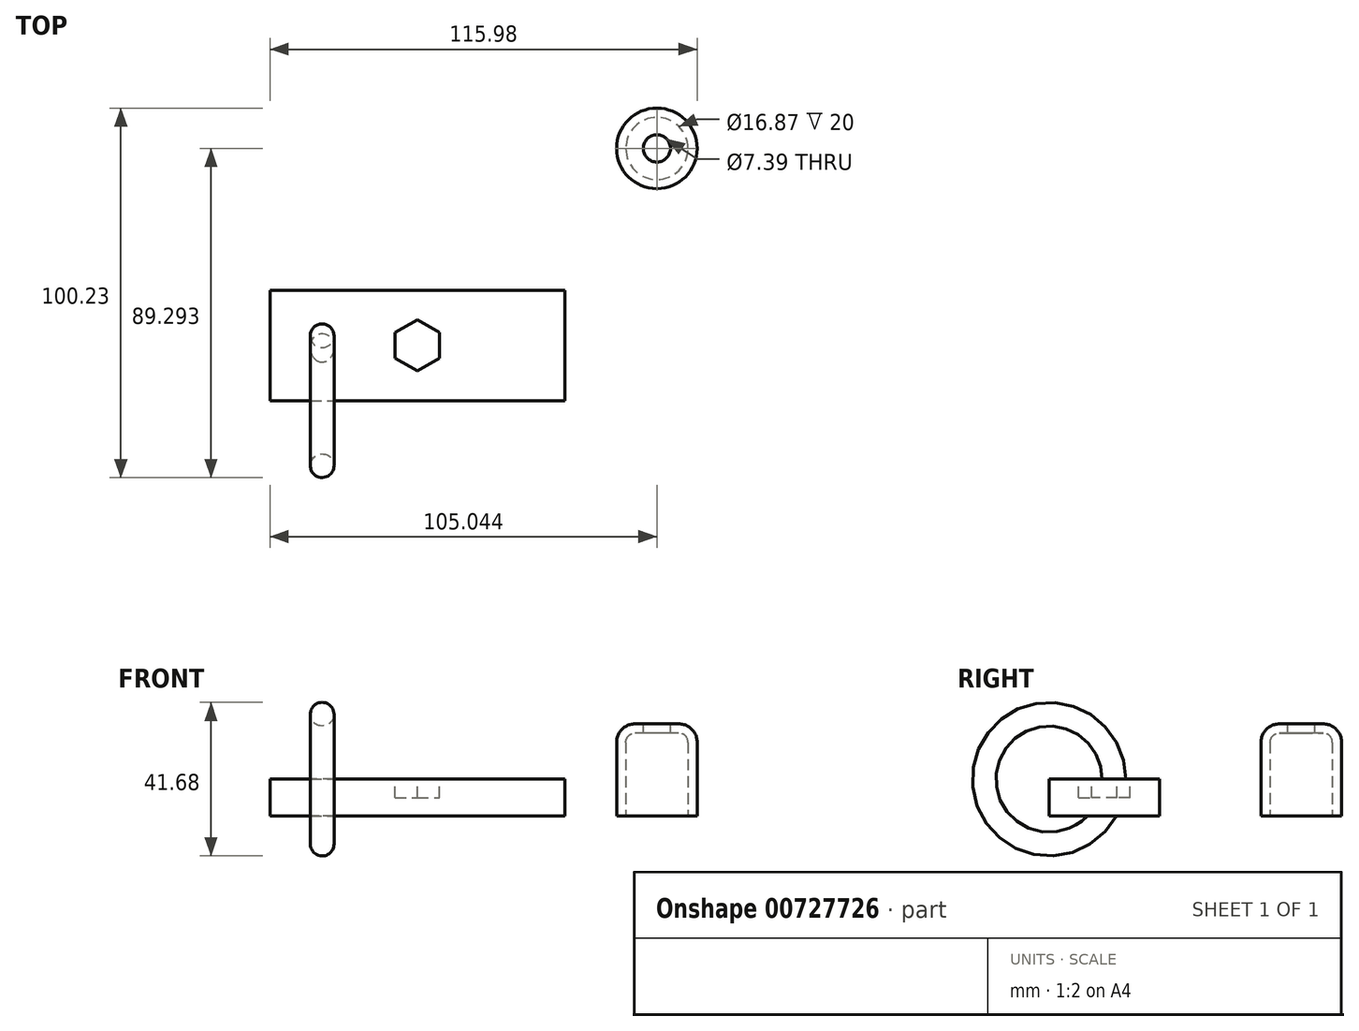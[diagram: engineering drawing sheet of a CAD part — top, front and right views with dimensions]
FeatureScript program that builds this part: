
annotation { "Feature Type Name" : "Feature", "Feature Type Description" : "" }
export const myFeature = defineFeature(function(context is Context, id is Id, definition is map)
    precondition{}
    {
        {
            var Q0;
            Q0=qCreatedBy(makeId("Top.planeOp"),FACE);
            var sketch = newSketch(context, id + "F0", { "sketchPlane" : qUnion([Q0])});
            skLineSegment(sketch, "E0.bottom", {"start": v(-40, -15) * mm, "end": v(40, -15) * mm});
            skLineSegment(sketch, "E0.top", {"start": v(-40, 15) * mm, "end": v(40, 15) * mm});
            skLineSegment(sketch, "E0.left", {"start": v(-40, -15) * mm, "end": v(-40, 15) * mm});
            skLineSegment(sketch, "E0.right", {"start": v(40, -15) * mm, "end": v(40, 15) * mm});
            skPoint(sketch, "E1", {"position": v(-40, 0) * mm});
            skPoint(sketch, "E2", {"position": v(0, -15) * mm});
            skSolve(sketch);
        }
        {
            var Q0;
            Q0=makeQuery(id+"F0.imprint","IMPRINT",FACE,{"disambiguationData":[TD([[makeQuery(id+"F0.imprint","IMPRINT",EDGE,{"derivedFrom":sQuery(id+"F0.wireOp",EDGE,"E0.bottom")}),1.0]])]});
            extrude(context, id + "F1", {"entities" : qUnion([Q0]), "depth" : 10 * mm, "offsetDistance" : 25 * mm});
        }
        {
            var Q0;
            Q0=makeQuery(id+"F1.opExtrude","CAP_FACE",FACE,{"disambiguationData":[OSD([sQuery(id+"F0.wireOp",EDGE,"E0.bottom"),sQuery(id+"F0.wireOp",EDGE,"E0.top"),sQuery(id+"F0.wireOp",EDGE,"E0.left"),sQuery(id+"F0.wireOp",EDGE,"E0.right")])],"isStart":false});
            var sketch = newSketch(context, id + "F2", { "sketchPlane" : qUnion([Q0])});
            skCircle(sketch, "E3.cCircle", {"center": v(0, 0) * mm, "radius": 6 * mm, "construction": true});
            skLineSegment(sketch, "E3.0", {"start": v(6, 3.46) * mm, "end": v(6, -3.46) * mm});
            skLineSegment(sketch, "E3.1", {"start": v(6, -3.46) * mm, "end": v(0, -6.93) * mm});
            skLineSegment(sketch, "E3.2", {"start": v(0, -6.93) * mm, "end": v(-6, -3.46) * mm});
            skLineSegment(sketch, "E3.3", {"start": v(-6, -3.46) * mm, "end": v(-6, 3.46) * mm});
            skLineSegment(sketch, "E3.4", {"start": v(-6, 3.46) * mm, "end": v(0, 6.93) * mm});
            skLineSegment(sketch, "E3.5", {"start": v(0, 6.93) * mm, "end": v(6, 3.46) * mm});
            skPoint(sketch, "E3.0.midPoint", {"position": v(6, 0) * mm});
            skSolve(sketch);
        }
        {
            var Q0;
            Q0=makeQuery(id+"F2.imprint","IMPRINT",FACE,{"disambiguationData":[TD([[makeQuery(id+"F2.imprint","IMPRINT",EDGE,{"derivedFrom":sQuery(id+"F2.wireOp",EDGE,"E3.0")}),-1.0]])]});
            extrude(context, id + "F3", {"entities" : qUnion([Q0]), "operationType" : NewBodyOperationType.REMOVE, "oppositeDirection" : true, "depth" : 5 * mm, "offsetDistance" : 25 * mm});
        }
        {
            var Q0;
            Q0=makeQuery(id+"F1.opExtrude","CAP_FACE",FACE,{"disambiguationData":[OSD([sQuery(id+"F0.wireOp",EDGE,"E0.bottom"),sQuery(id+"F0.wireOp",EDGE,"E0.top"),sQuery(id+"F0.wireOp",EDGE,"E0.left"),sQuery(id+"F0.wireOp",EDGE,"E0.right")])],"isStart":false});
            var sketch = newSketch(context, id + "F4", { "sketchPlane" : qUnion([Q0])});
            skCircle(sketch, "E4", {"center": v(-25.82, 2.63) * mm, "radius": 3.21 * mm});
            skSolve(sketch);
        }
        {
            var Q0;
            Q0=makeQuery(id+"F4.imprint","IMPRINT",FACE,{"disambiguationData":[TD([[makeQuery(id+"F4.imprint","IMPRINT",EDGE,{"derivedFrom":sQuery(id+"F4.wireOp",EDGE,"E4")}),1.0]])]});
            var Q1;
            Q1=makeQuery(id+"F1.opExtrude","CAP_EDGE",EDGE,{"disambiguationData":[OSD([sQuery(id+"F0.wireOp",EDGE,"E0.bottom")])],"isStart":false});
            revolve(context, id + "F5", {"operationType" : NewBodyOperationType.ADD, "surfaceOperationType" : NewSurfaceOperationType.NEW, "entities" : qUnion([Q0]), "axis" : qUnion([Q1]), "revolveType" : RevolveType.FULL});
        }
        {
            var Q0;
            Q0=qCreatedBy(makeId("Top.planeOp"),FACE);
            var sketch = newSketch(context, id + "F6", { "sketchPlane" : qUnion([Q0])});
            skCircle(sketch, "E5", {"center": v(65.04, 53.45) * mm, "radius": 10.94 * mm});
            skSolve(sketch);
        }
        {
            var Q0;
            Q0=makeQuery(id+"F6.imprint","IMPRINT",FACE,{"disambiguationData":[TD([[makeQuery(id+"F6.imprint","IMPRINT",EDGE,{"derivedFrom":sQuery(id+"F6.wireOp",EDGE,"E5")}),1.0]])]});
            extrude(context, id + "F7", {"entities" : qUnion([Q0]), "depth" : 25 * mm, "offsetDistance" : 25 * mm});
        }
        {
            var Q0;
            Q0=makeQuery(id+"F7.opExtrude","CAP_EDGE",EDGE,{"disambiguationData":[OSD([sQuery(id+"F6.wireOp",EDGE,"E5")])],"isStart":false});
            fillet(context, id + "F8", {"entities" : qUnion([Q0]), "radius" : 5 * mm, "tangentPropagation" : true, "allowEdgeOverflow" : false});
        }
        {
            var Q0;
            Q0=makeQuery(id+"F7.opExtrude","CAP_FACE",FACE,{"disambiguationData":[OSD([sQuery(id+"F6.wireOp",EDGE,"E5")])],"isStart":true});
            shell(context, id + "F9", {"entities" : qUnion([Q0]), "thickness" : 2.5 * mm});
        }
        {
            var Q0;
            Q0=makeQuery(id+"F7.opExtrude","CAP_FACE",FACE,{"disambiguationData":[OSD([sQuery(id+"F6.wireOp",EDGE,"E5")])],"isStart":false});
            var sketch = newSketch(context, id + "F10", { "sketchPlane" : qUnion([Q0])});
            skCircle(sketch, "E6", {"center": v(65.04, 53.45) * mm, "radius": 3.7 * mm});
            skSolve(sketch);
        }
        {
            var Q0;
            Q0=makeQuery(id+"F10.imprint","IMPRINT",FACE,{"disambiguationData":[TD([[makeQuery(id+"F10.imprint","IMPRINT",EDGE,{"derivedFrom":sQuery(id+"F10.wireOp",EDGE,"E6")}),1.0]])]});
            extrude(context, id + "F11", {"entities" : qUnion([Q0]), "operationType" : NewBodyOperationType.REMOVE, "oppositeDirection" : true, "depth" : 25 * mm, "offsetDistance" : 25 * mm});
        }
    });
